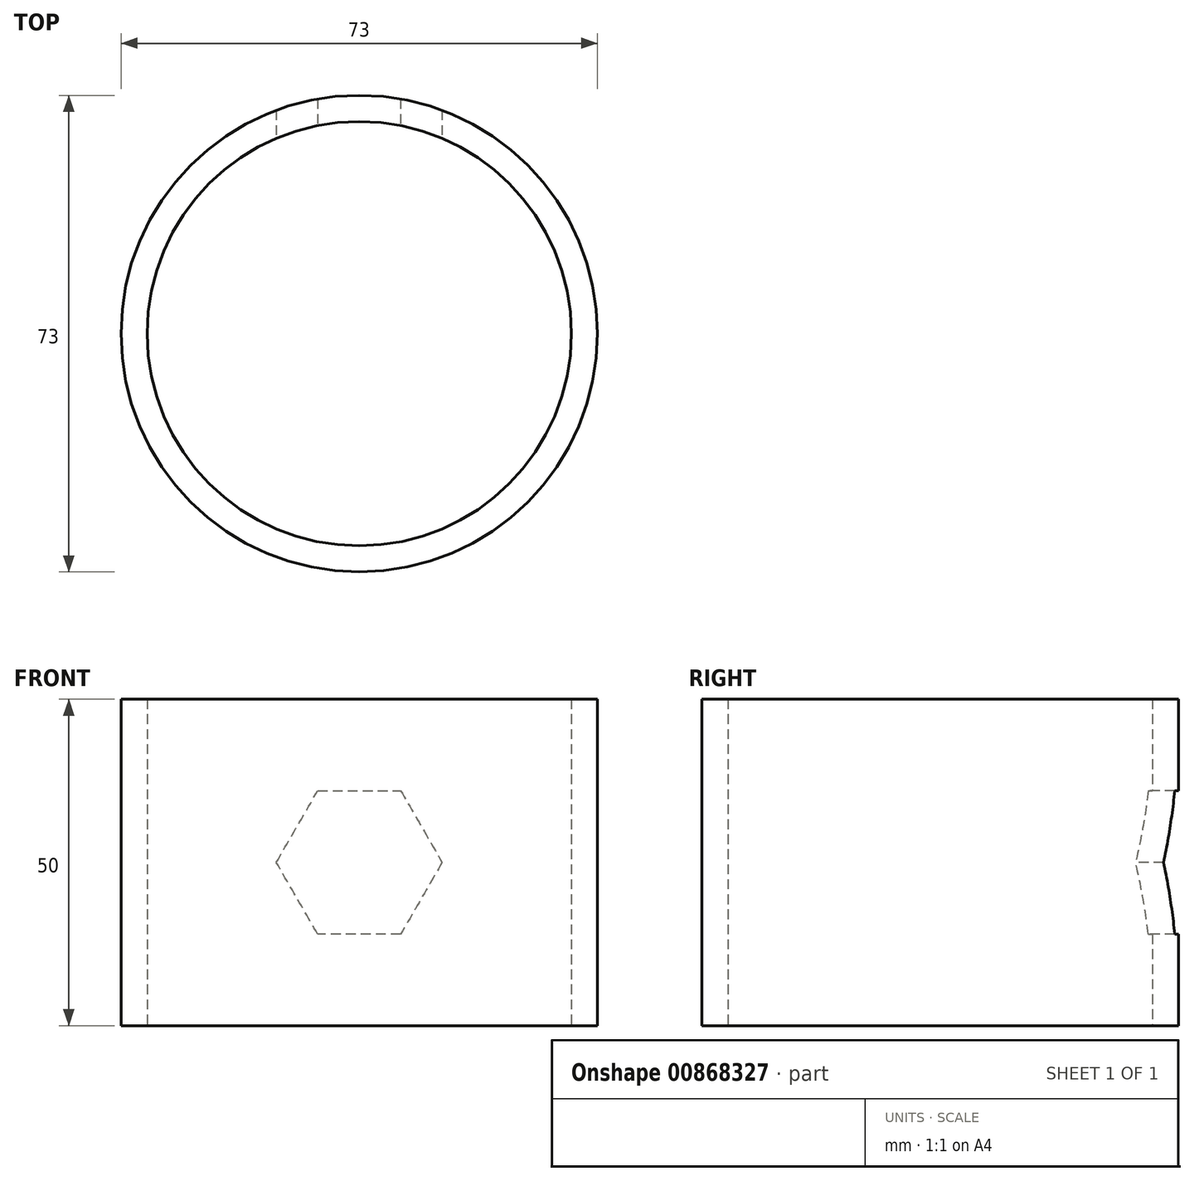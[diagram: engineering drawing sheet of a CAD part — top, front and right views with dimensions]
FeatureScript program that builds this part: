
annotation { "Feature Type Name" : "Feature", "Feature Type Description" : "" }
export const myFeature = defineFeature(function(context is Context, id is Id, definition is map)
    precondition{}
    {
        {
            var Q0;
            Q0=qCreatedBy(makeId("Top.planeOp"),FACE);
            var sketch = newSketch(context, id + "F0", { "sketchPlane" : qUnion([Q0])});
            skCircle(sketch, "E0", {"center": v(0, 0) * mm, "radius": 36.5 * mm});
            skCircle(sketch, "E1", {"center": v(0, 0) * mm, "radius": 32.5 * mm});
            skSolve(sketch);
        }
        {
            var Q0;
            Q0=makeQuery(id+"F0.imprint","IMPRINT",FACE,{"disambiguationData":[TD([[makeQuery(id+"F0.imprint","IMPRINT",EDGE,{"derivedFrom":sQuery(id+"F0.wireOp",EDGE,"E0")}),1.0]])]});
            extrude(context, id + "F1", {"entities" : qUnion([Q0]), "endBound" : BoundingType.SYMMETRIC, "depth" : 50 * mm, "offsetDistance" : 25 * mm});
        }
        {
            var Q0;
            Q0=qCreatedBy(makeId("Front.planeOp"),FACE);
            var sketch = newSketch(context, id + "F2", { "sketchPlane" : qUnion([Q0])});
            skCircle(sketch, "E2.cCircle", {"center": v(0, 0) * mm, "radius": 11 * mm, "construction": true});
            skLineSegment(sketch, "E2.0", {"start": v(6.35, -11) * mm, "end": v(-6.35, -11) * mm});
            skLineSegment(sketch, "E2.1", {"start": v(-6.35, -11) * mm, "end": v(-12.7, 0) * mm});
            skLineSegment(sketch, "E2.2", {"start": v(-12.7, 0) * mm, "end": v(-6.35, 11) * mm});
            skLineSegment(sketch, "E2.3", {"start": v(-6.35, 11) * mm, "end": v(6.35, 11) * mm});
            skLineSegment(sketch, "E2.4", {"start": v(6.35, 11) * mm, "end": v(12.7, 0) * mm});
            skLineSegment(sketch, "E2.5", {"start": v(12.7, 0) * mm, "end": v(6.35, -11) * mm});
            skPoint(sketch, "E2.0.midPoint", {"position": v(0, -11) * mm});
            skSolve(sketch);
        }
        {
            var Q0;
            Q0=makeQuery(id+"F2.imprint","IMPRINT",FACE,{"disambiguationData":[TD([[makeQuery(id+"F2.imprint","IMPRINT",EDGE,{"derivedFrom":sQuery(id+"F2.wireOp",EDGE,"e3572ce9-97d7-4778-97bc-65f67125c358.0")}),-1.0]])]});
            var Q1;
            Q1=makeQuery(id+"F2.imprint","IMPRINT",FACE,{"disambiguationData":[TD([[makeQuery(id+"F2.imprint","IMPRINT",EDGE,{"derivedFrom":sQuery(id+"F2.wireOp",EDGE,"E2.0")}),-1.0]])]});
            extrude(context, id + "F3", {"entities" : qUnion([Q0, Q1]), "operationType" : NewBodyOperationType.REMOVE, "oppositeDirection" : true, "depth" : 40 * mm, "offsetDistance" : 25 * mm});
        }
    });
